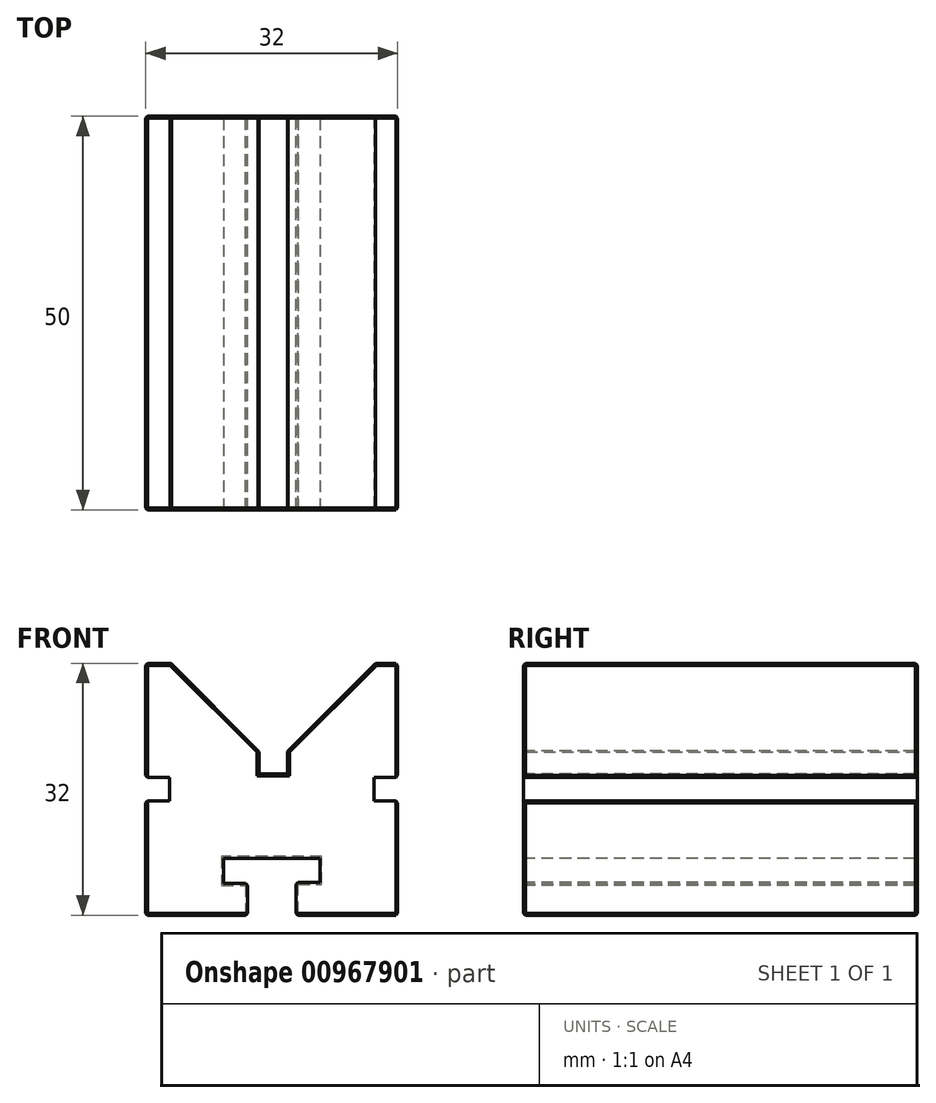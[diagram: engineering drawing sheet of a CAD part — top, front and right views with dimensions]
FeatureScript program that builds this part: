
annotation { "Feature Type Name" : "Feature", "Feature Type Description" : "" }
export const myFeature = defineFeature(function(context is Context, id is Id, definition is map)
    precondition{}
    {
        {
            var Q0;
            Q0=qCreatedBy(makeId("Front.planeOp"),FACE);
            var sketch = newSketch(context, id + "F0", { "sketchPlane" : qUnion([Q0])});
            skLineSegment(sketch, "E0", {"start": v(0, 0) * mm, "end": v(32, 0) * mm});
            skLineSegment(sketch, "E1", {"start": v(32, 0) * mm, "end": v(32, 32) * mm});
            skLineSegment(sketch, "E2", {"start": v(32, 32) * mm, "end": v(29.18, 32) * mm});
            skLineSegment(sketch, "E3", {"start": v(29.18, 32) * mm, "end": v(18, 20.82) * mm});
            skLineSegment(sketch, "E4", {"start": v(18, 20.82) * mm, "end": v(18, 17.96) * mm});
            skLineSegment(sketch, "E5", {"start": v(18, 17.96) * mm, "end": v(14.36, 17.96) * mm});
            skLineSegment(sketch, "E6", {"start": v(14.36, 17.96) * mm, "end": v(14.36, 20.82) * mm});
            skLineSegment(sketch, "E7", {"start": v(14.36, 20.82) * mm, "end": v(3.18, 32) * mm});
            skLineSegment(sketch, "E8", {"start": v(3.18, 32) * mm, "end": v(0, 32) * mm});
            skLineSegment(sketch, "E9", {"start": v(0, 32) * mm, "end": v(0, 0) * mm});
            skLineSegment(sketch, "E10", {"start": v(29.18, 32) * mm, "end": v(16.18, 19) * mm});
            skLineSegment(sketch, "E11", {"start": v(16.18, 19) * mm, "end": v(3.18, 32) * mm});
            skLineSegment(sketch, "E12", {"start": v(3.24, 35.24) * mm, "end": v(0, 32) * mm});
            skSolve(sketch);
        }
        {
            var Q0;
            Q0=makeQuery(id+"F0.imprint","IMPRINT",FACE,{"disambiguationData":[TD([[makeQuery(id+"F0.imprint","IMPRINT",EDGE,{"derivedFrom":sQuery(id+"F0.wireOp",EDGE,"E0")}),1.0]])]});
            extrude(context, id + "F1", {"entities" : qUnion([Q0]), "oppositeDirection" : true, "depth" : 50 * mm, "offsetDistance" : 25 * mm});
        }
        {
            var Q0;
            Q0=qCreatedBy(makeId("Front.planeOp"),FACE);
            var sketch = newSketch(context, id + "F2", { "sketchPlane" : qUnion([Q0])});
            skLineSegment(sketch, "E13", {"start": v(9.9, 7.2) * mm, "end": v(22.1, 7.2) * mm});
            skLineSegment(sketch, "E14", {"start": v(22.1, 7.2) * mm, "end": v(22.1, 4.2) * mm});
            skLineSegment(sketch, "E15", {"start": v(22.1, 4.2) * mm, "end": v(19.1, 4.2) * mm});
            skLineSegment(sketch, "E16", {"start": v(19.1, 4.2) * mm, "end": v(19.1, -5.87) * mm});
            skLineSegment(sketch, "E17", {"start": v(19.1, -5.87) * mm, "end": v(12.9, -5.87) * mm});
            skLineSegment(sketch, "E18", {"start": v(12.9, -5.87) * mm, "end": v(12.9, 4.07) * mm});
            skLineSegment(sketch, "E19", {"start": v(12.9, 4.07) * mm, "end": v(9.9, 4.07) * mm});
            skLineSegment(sketch, "E20", {"start": v(9.9, 4.07) * mm, "end": v(9.9, 7.2) * mm});
            skSolve(sketch);
        }
        {
            var Q0;
            Q0 = qSketchRegion(id + "F2", true);
            extrude(context, id + "F3", {"entities" : qUnion([Q0]), "operationType" : NewBodyOperationType.REMOVE, "oppositeDirection" : true, "depth" : 55 * mm, "offsetDistance" : 25 * mm});
        }
        {
            var Q0;
            Q0=qCreatedBy(makeId("Front.planeOp"),FACE);
            var sketch = newSketch(context, id + "F4", { "sketchPlane" : qUnion([Q0])});
            skLineSegment(sketch, "E21", {"start": v(29, 17.5) * mm, "end": v(29, 14.5) * mm});
            skLineSegment(sketch, "E22", {"start": v(29, 14.5) * mm, "end": v(35.37, 14.5) * mm});
            skLineSegment(sketch, "E23", {"start": v(35.37, 14.5) * mm, "end": v(35.37, 17.5) * mm});
            skLineSegment(sketch, "E24", {"start": v(35.37, 17.5) * mm, "end": v(29, 17.5) * mm});
            skLineSegment(sketch, "E25", {"start": v(-2.73, 17.5) * mm, "end": v(3, 17.5) * mm});
            skLineSegment(sketch, "E26", {"start": v(3, 17.5) * mm, "end": v(3, 14.5) * mm});
            skLineSegment(sketch, "E27", {"start": v(3, 14.5) * mm, "end": v(-2.73, 14.5) * mm});
            skLineSegment(sketch, "E28", {"start": v(-2.73, 14.5) * mm, "end": v(-2.73, 17.5) * mm});
            skSolve(sketch);
        }
        {
            var Q0;
            Q0 = qSketchRegion(id + "F4", true);
            extrude(context, id + "F5", {"entities" : qUnion([Q0]), "operationType" : NewBodyOperationType.REMOVE, "oppositeDirection" : true, "depth" : 50 * mm, "offsetDistance" : 25 * mm});
        }
        {
            var Q0;
            Q0=makeQuery(id+"F1.opExtrude","SWEPT_EDGE",EDGE,{"disambiguationData":[OSD([sQuery(id+"F0.wireOp",EDGE,"E1"),sQuery(id+"F0.wireOp",EDGE,"E2")])]});
            var Q1;
            {var subQ0=sQuery(id+"F0.wireOp",EDGE,"E2");var subQ1=sQuery(id+"F0.wireOp",EDGE,"E1");Q1=makeQuery(id+"F5.boolean.opBoolean","SPLIT",EDGE,{"disambiguationData":[TD([makeQuery(id+"F1.opExtrude","SWEPT_FACE",FACE,{"disambiguationData":[OSD([subQ0])]})])],"derivedFrom":makeQuery(id+"F1.opExtrude","CAP_EDGE",EDGE,{"disambiguationData":[OSD([subQ1])],"isStart":false})});}
            var Q2;
            {var subQ0=sQuery(id+"F0.wireOp",EDGE,"E0");var subQ1=sQuery(id+"F0.wireOp",EDGE,"E1");Q2=makeQuery(id+"F5.boolean.opBoolean","SPLIT",EDGE,{"disambiguationData":[TD([makeQuery(id+"F1.opExtrude","SWEPT_FACE",FACE,{"disambiguationData":[OSD([subQ0])]})])],"derivedFrom":makeQuery(id+"F1.opExtrude","CAP_EDGE",EDGE,{"disambiguationData":[OSD([subQ1])],"isStart":false})});}
            var Q3;
            Q3=makeQuery(id+"F1.opExtrude","SWEPT_EDGE",EDGE,{"disambiguationData":[OSD([sQuery(id+"F0.wireOp",EDGE,"E0"),sQuery(id+"F0.wireOp",EDGE,"E1")])]});
            var Q4;
            {var subQ0=sQuery(id+"F0.wireOp",EDGE,"E0");var subQ1=sQuery(id+"F0.wireOp",EDGE,"E1");Q4=makeQuery(id+"F5.boolean.opBoolean","SPLIT",EDGE,{"disambiguationData":[TD([makeQuery(id+"F1.opExtrude","SWEPT_FACE",FACE,{"disambiguationData":[OSD([subQ0])]})])],"derivedFrom":makeQuery(id+"F1.opExtrude","CAP_EDGE",EDGE,{"disambiguationData":[OSD([subQ1])],"isStart":true})});}
            var Q5;
            {var subQ0=sQuery(id+"F0.wireOp",EDGE,"E2");var subQ1=sQuery(id+"F0.wireOp",EDGE,"E1");Q5=makeQuery(id+"F5.boolean.opBoolean","SPLIT",EDGE,{"disambiguationData":[TD([makeQuery(id+"F1.opExtrude","SWEPT_FACE",FACE,{"disambiguationData":[OSD([subQ0])]})])],"derivedFrom":makeQuery(id+"F1.opExtrude","CAP_EDGE",EDGE,{"disambiguationData":[OSD([subQ1])],"isStart":true})});}
            var Q6;
            Q6=makeQuery(id+"F5.boolean.opBoolean","INTERSECT",EDGE,{"derivedFrom":[makeQuery(id+"F1.opExtrude","SWEPT_FACE",FACE,{"disambiguationData":[OSD([sQuery(id+"F0.wireOp",EDGE,"E1")])]}),makeQuery(id+"F5.opExtrude","SWEPT_FACE",FACE,{"disambiguationData":[OSD([sQuery(id+"F4.wireOp",EDGE,"E24")])]})]});
            var Q7;
            Q7=makeQuery(id+"F5.boolean.opBoolean","INTERSECT",EDGE,{"derivedFrom":[makeQuery(id+"F1.opExtrude","SWEPT_FACE",FACE,{"disambiguationData":[OSD([sQuery(id+"F0.wireOp",EDGE,"E1")])]}),makeQuery(id+"F5.opExtrude","SWEPT_FACE",FACE,{"disambiguationData":[OSD([sQuery(id+"F4.wireOp",EDGE,"E22")])]})]});
            var Q8;
            Q8=makeQuery(id+"F5.boolean.opBoolean","COPY",EDGE,{"derivedFrom":makeQuery(id+"F5.opExtrude","CAP_EDGE",EDGE,{"disambiguationData":[OSD([sQuery(id+"F4.wireOp",EDGE,"E24")])],"isStart":false})});
            var Q9;
            Q9=makeQuery(id+"F5.boolean.opBoolean","COPY",EDGE,{"derivedFrom":makeQuery(id+"F5.opExtrude","CAP_EDGE",EDGE,{"disambiguationData":[OSD([sQuery(id+"F4.wireOp",EDGE,"E22")])],"isStart":false})});
            var Q10;
            Q10=makeQuery(id+"F5.boolean.opBoolean","COPY",EDGE,{"derivedFrom":makeQuery(id+"F5.opExtrude","CAP_EDGE",EDGE,{"disambiguationData":[OSD([sQuery(id+"F4.wireOp",EDGE,"E21")])],"isStart":false})});
            var Q11;
            {var subQ0=sQuery(id+"F0.wireOp",EDGE,"E0");var subQ1=sQuery(id+"F0.wireOp",EDGE,"E1");Q11=makeQuery(id+"F3.boolean.opBoolean","SPLIT",EDGE,{"disambiguationData":[TD([makeQuery(id+"F1.opExtrude","SWEPT_FACE",FACE,{"disambiguationData":[OSD([subQ1])]})])],"derivedFrom":makeQuery(id+"F1.opExtrude","CAP_EDGE",EDGE,{"disambiguationData":[OSD([subQ0])],"isStart":false})});}
            var Q12;
            Q12=makeQuery(id+"F3.boolean.opBoolean","INTERSECT",EDGE,{"derivedFrom":[makeQuery(id+"F1.opExtrude","CAP_FACE",FACE,{"disambiguationData":[OSD([sQuery(id+"F0.wireOp",EDGE,"E0"),sQuery(id+"F0.wireOp",EDGE,"E1"),sQuery(id+"F0.wireOp",EDGE,"E2"),sQuery(id+"F0.wireOp",EDGE,"E3"),sQuery(id+"F0.wireOp",EDGE,"E4"),sQuery(id+"F0.wireOp",EDGE,"E5"),sQuery(id+"F0.wireOp",EDGE,"E6"),sQuery(id+"F0.wireOp",EDGE,"E7"),sQuery(id+"F0.wireOp",EDGE,"E8"),sQuery(id+"F0.wireOp",EDGE,"E9")])],"isStart":false}),makeQuery(id+"F3.opExtrude","SWEPT_FACE",FACE,{"disambiguationData":[OSD([sQuery(id+"F2.wireOp",EDGE,"E14")])]})]});
            var Q13;
            Q13=makeQuery(id+"F3.boolean.opBoolean","INTERSECT",EDGE,{"derivedFrom":[makeQuery(id+"F1.opExtrude","CAP_FACE",FACE,{"disambiguationData":[OSD([sQuery(id+"F0.wireOp",EDGE,"E0"),sQuery(id+"F0.wireOp",EDGE,"E1"),sQuery(id+"F0.wireOp",EDGE,"E2"),sQuery(id+"F0.wireOp",EDGE,"E3"),sQuery(id+"F0.wireOp",EDGE,"E4"),sQuery(id+"F0.wireOp",EDGE,"E5"),sQuery(id+"F0.wireOp",EDGE,"E6"),sQuery(id+"F0.wireOp",EDGE,"E7"),sQuery(id+"F0.wireOp",EDGE,"E8"),sQuery(id+"F0.wireOp",EDGE,"E9")])],"isStart":false}),makeQuery(id+"F3.opExtrude","SWEPT_FACE",FACE,{"disambiguationData":[OSD([sQuery(id+"F2.wireOp",EDGE,"E13")])]})]});
            var Q14;
            Q14=makeQuery(id+"F3.boolean.opBoolean","INTERSECT",EDGE,{"derivedFrom":[makeQuery(id+"F1.opExtrude","CAP_FACE",FACE,{"disambiguationData":[OSD([sQuery(id+"F0.wireOp",EDGE,"E0"),sQuery(id+"F0.wireOp",EDGE,"E1"),sQuery(id+"F0.wireOp",EDGE,"E2"),sQuery(id+"F0.wireOp",EDGE,"E3"),sQuery(id+"F0.wireOp",EDGE,"E4"),sQuery(id+"F0.wireOp",EDGE,"E5"),sQuery(id+"F0.wireOp",EDGE,"E6"),sQuery(id+"F0.wireOp",EDGE,"E7"),sQuery(id+"F0.wireOp",EDGE,"E8"),sQuery(id+"F0.wireOp",EDGE,"E9")])],"isStart":false}),makeQuery(id+"F3.opExtrude","SWEPT_FACE",FACE,{"disambiguationData":[OSD([sQuery(id+"F2.wireOp",EDGE,"E20")])]})]});
            var Q15;
            Q15=makeQuery(id+"F3.boolean.opBoolean","INTERSECT",EDGE,{"derivedFrom":[makeQuery(id+"F1.opExtrude","CAP_FACE",FACE,{"disambiguationData":[OSD([sQuery(id+"F0.wireOp",EDGE,"E0"),sQuery(id+"F0.wireOp",EDGE,"E1"),sQuery(id+"F0.wireOp",EDGE,"E2"),sQuery(id+"F0.wireOp",EDGE,"E3"),sQuery(id+"F0.wireOp",EDGE,"E4"),sQuery(id+"F0.wireOp",EDGE,"E5"),sQuery(id+"F0.wireOp",EDGE,"E6"),sQuery(id+"F0.wireOp",EDGE,"E7"),sQuery(id+"F0.wireOp",EDGE,"E8"),sQuery(id+"F0.wireOp",EDGE,"E9")])],"isStart":false}),makeQuery(id+"F3.opExtrude","SWEPT_FACE",FACE,{"disambiguationData":[OSD([sQuery(id+"F2.wireOp",EDGE,"E19")])]})]});
            var Q16;
            Q16=makeQuery(id+"F3.boolean.opBoolean","INTERSECT",EDGE,{"derivedFrom":[makeQuery(id+"F1.opExtrude","CAP_FACE",FACE,{"disambiguationData":[OSD([sQuery(id+"F0.wireOp",EDGE,"E0"),sQuery(id+"F0.wireOp",EDGE,"E1"),sQuery(id+"F0.wireOp",EDGE,"E2"),sQuery(id+"F0.wireOp",EDGE,"E3"),sQuery(id+"F0.wireOp",EDGE,"E4"),sQuery(id+"F0.wireOp",EDGE,"E5"),sQuery(id+"F0.wireOp",EDGE,"E6"),sQuery(id+"F0.wireOp",EDGE,"E7"),sQuery(id+"F0.wireOp",EDGE,"E8"),sQuery(id+"F0.wireOp",EDGE,"E9")])],"isStart":false}),makeQuery(id+"F3.opExtrude","SWEPT_FACE",FACE,{"disambiguationData":[OSD([sQuery(id+"F2.wireOp",EDGE,"E18")])]})]});
            var Q17;
            Q17=makeQuery(id+"F3.boolean.opBoolean","INTERSECT",EDGE,{"derivedFrom":[makeQuery(id+"F1.opExtrude","CAP_FACE",FACE,{"disambiguationData":[OSD([sQuery(id+"F0.wireOp",EDGE,"E0"),sQuery(id+"F0.wireOp",EDGE,"E1"),sQuery(id+"F0.wireOp",EDGE,"E2"),sQuery(id+"F0.wireOp",EDGE,"E3"),sQuery(id+"F0.wireOp",EDGE,"E4"),sQuery(id+"F0.wireOp",EDGE,"E5"),sQuery(id+"F0.wireOp",EDGE,"E6"),sQuery(id+"F0.wireOp",EDGE,"E7"),sQuery(id+"F0.wireOp",EDGE,"E8"),sQuery(id+"F0.wireOp",EDGE,"E9")])],"isStart":false}),makeQuery(id+"F3.opExtrude","SWEPT_FACE",FACE,{"disambiguationData":[OSD([sQuery(id+"F2.wireOp",EDGE,"E16")])]})]});
            var Q18;
            Q18=makeQuery(id+"F3.boolean.opBoolean","INTERSECT",EDGE,{"derivedFrom":[makeQuery(id+"F1.opExtrude","CAP_FACE",FACE,{"disambiguationData":[OSD([sQuery(id+"F0.wireOp",EDGE,"E0"),sQuery(id+"F0.wireOp",EDGE,"E1"),sQuery(id+"F0.wireOp",EDGE,"E2"),sQuery(id+"F0.wireOp",EDGE,"E3"),sQuery(id+"F0.wireOp",EDGE,"E4"),sQuery(id+"F0.wireOp",EDGE,"E5"),sQuery(id+"F0.wireOp",EDGE,"E6"),sQuery(id+"F0.wireOp",EDGE,"E7"),sQuery(id+"F0.wireOp",EDGE,"E8"),sQuery(id+"F0.wireOp",EDGE,"E9")])],"isStart":false}),makeQuery(id+"F3.opExtrude","SWEPT_FACE",FACE,{"disambiguationData":[OSD([sQuery(id+"F2.wireOp",EDGE,"E15")])]})]});
            var Q19;
            {var subQ0=sQuery(id+"F0.wireOp",EDGE,"E0");var subQ1=sQuery(id+"F0.wireOp",EDGE,"E9");Q19=makeQuery(id+"F3.boolean.opBoolean","SPLIT",EDGE,{"disambiguationData":[TD([makeQuery(id+"F1.opExtrude","SWEPT_FACE",FACE,{"disambiguationData":[OSD([subQ1])]})])],"derivedFrom":makeQuery(id+"F1.opExtrude","CAP_EDGE",EDGE,{"disambiguationData":[OSD([subQ0])],"isStart":false})});}
            var Q20;
            {var subQ0=sQuery(id+"F0.wireOp",EDGE,"E0");var subQ1=sQuery(id+"F0.wireOp",EDGE,"E9");Q20=makeQuery(id+"F5.boolean.opBoolean","SPLIT",EDGE,{"disambiguationData":[TD([makeQuery(id+"F1.opExtrude","SWEPT_FACE",FACE,{"disambiguationData":[OSD([subQ0])]})])],"derivedFrom":makeQuery(id+"F1.opExtrude","CAP_EDGE",EDGE,{"disambiguationData":[OSD([subQ1])],"isStart":false})});}
            var Q21;
            Q21=makeQuery(id+"F1.opExtrude","SWEPT_EDGE",EDGE,{"disambiguationData":[OSD([sQuery(id+"F0.wireOp",EDGE,"E0"),sQuery(id+"F0.wireOp",EDGE,"E9")])]});
            var Q22;
            {var subQ0=sQuery(id+"F0.wireOp",EDGE,"E0");var subQ1=sQuery(id+"F0.wireOp",EDGE,"E9");Q22=makeQuery(id+"F5.boolean.opBoolean","SPLIT",EDGE,{"disambiguationData":[TD([makeQuery(id+"F1.opExtrude","SWEPT_FACE",FACE,{"disambiguationData":[OSD([subQ0])]})])],"derivedFrom":makeQuery(id+"F1.opExtrude","CAP_EDGE",EDGE,{"disambiguationData":[OSD([subQ1])],"isStart":true})});}
            var Q23;
            Q23=makeQuery(id+"F5.boolean.opBoolean","INTERSECT",EDGE,{"derivedFrom":[makeQuery(id+"F1.opExtrude","SWEPT_FACE",FACE,{"disambiguationData":[OSD([sQuery(id+"F0.wireOp",EDGE,"E9")])]}),makeQuery(id+"F5.opExtrude","SWEPT_FACE",FACE,{"disambiguationData":[OSD([sQuery(id+"F4.wireOp",EDGE,"E27")])]})]});
            var Q24;
            Q24=makeQuery(id+"F5.boolean.opBoolean","COPY",EDGE,{"derivedFrom":makeQuery(id+"F5.opExtrude","CAP_EDGE",EDGE,{"disambiguationData":[OSD([sQuery(id+"F4.wireOp",EDGE,"E25")])],"isStart":false})});
            var Q25;
            Q25=makeQuery(id+"F5.boolean.opBoolean","COPY",EDGE,{"derivedFrom":makeQuery(id+"F5.opExtrude","CAP_EDGE",EDGE,{"disambiguationData":[OSD([sQuery(id+"F4.wireOp",EDGE,"E26")])],"isStart":false})});
            var Q26;
            Q26=makeQuery(id+"F5.boolean.opBoolean","COPY",EDGE,{"derivedFrom":makeQuery(id+"F5.opExtrude","CAP_EDGE",EDGE,{"disambiguationData":[OSD([sQuery(id+"F4.wireOp",EDGE,"E27")])],"isStart":false})});
            var Q27;
            {var subQ0=sQuery(id+"F0.wireOp",EDGE,"E9");var subQ1=sQuery(id+"F0.wireOp",EDGE,"E8");Q27=makeQuery(id+"F5.boolean.opBoolean","SPLIT",EDGE,{"disambiguationData":[TD([makeQuery(id+"F1.opExtrude","SWEPT_FACE",FACE,{"disambiguationData":[OSD([subQ1])]})])],"derivedFrom":makeQuery(id+"F1.opExtrude","CAP_EDGE",EDGE,{"disambiguationData":[OSD([subQ0])],"isStart":false})});}
            var Q28;
            Q28=makeQuery(id+"F1.opExtrude","CAP_EDGE",EDGE,{"disambiguationData":[OSD([sQuery(id+"F0.wireOp",EDGE,"E8")])],"isStart":false});
            var Q29;
            Q29=makeQuery(id+"F1.opExtrude","CAP_EDGE",EDGE,{"disambiguationData":[OSD([sQuery(id+"F0.wireOp",EDGE,"E7")])],"isStart":false});
            var Q30;
            Q30=makeQuery(id+"F1.opExtrude","CAP_EDGE",EDGE,{"disambiguationData":[OSD([sQuery(id+"F0.wireOp",EDGE,"E6")])],"isStart":false});
            var Q31;
            Q31=makeQuery(id+"F1.opExtrude","CAP_EDGE",EDGE,{"disambiguationData":[OSD([sQuery(id+"F0.wireOp",EDGE,"E5")])],"isStart":false});
            var Q32;
            Q32=makeQuery(id+"F1.opExtrude","CAP_EDGE",EDGE,{"disambiguationData":[OSD([sQuery(id+"F0.wireOp",EDGE,"E4")])],"isStart":false});
            var Q33;
            Q33=makeQuery(id+"F1.opExtrude","SWEPT_EDGE",EDGE,{"disambiguationData":[OSD([sQuery(id+"F0.wireOp",EDGE,"E3"),sQuery(id+"F0.wireOp",EDGE,"E4")])]});
            var Q34;
            Q34=makeQuery(id+"F1.opExtrude","CAP_EDGE",EDGE,{"disambiguationData":[OSD([sQuery(id+"F0.wireOp",EDGE,"E3")])],"isStart":false});
            var Q35;
            Q35=makeQuery(id+"F1.opExtrude","SWEPT_EDGE",EDGE,{"disambiguationData":[OSD([sQuery(id+"F0.wireOp",EDGE,"E8"),sQuery(id+"F0.wireOp",EDGE,"E9")])]});
            var Q36;
            Q36=makeQuery(id+"F1.opExtrude","SWEPT_EDGE",EDGE,{"disambiguationData":[OSD([sQuery(id+"F0.wireOp",EDGE,"E7"),sQuery(id+"F0.wireOp",EDGE,"E8")])]});
            var Q37;
            Q37=makeQuery(id+"F1.opExtrude","SWEPT_EDGE",EDGE,{"disambiguationData":[OSD([sQuery(id+"F0.wireOp",EDGE,"E6"),sQuery(id+"F0.wireOp",EDGE,"E7")])]});
            var Q38;
            Q38=makeQuery(id+"F1.opExtrude","CAP_EDGE",EDGE,{"disambiguationData":[OSD([sQuery(id+"F0.wireOp",EDGE,"E2")])],"isStart":false});
            chamfer(context, id + "F6", {"entities" : qUnion([Q0, Q1, Q2, Q3, Q4, Q5, Q6, Q7, Q8, Q9, Q10, Q11, Q12, Q13, Q14, Q15, Q16, Q17, Q18, Q19, Q20, Q21, Q22, Q23, Q24, Q25, Q26, Q27, Q28, Q29, Q30, Q31, Q32, Q33, Q34, Q35, Q36, Q37, Q38]), "width" : .25 * mm, "tangentPropagation" : true});
        }
        {
            var Q0;
            Q0=makeQuery(id+"F3.boolean.opBoolean","COPY",EDGE,{"derivedFrom":makeQuery(id+"F3.opExtrude","SWEPT_EDGE",EDGE,{"disambiguationData":[OSD([sQuery(id+"F2.wireOp",EDGE,"E15"),sQuery(id+"F2.wireOp",EDGE,"E16")])]})});
            var Q1;
            Q1=makeQuery(id+"F3.boolean.opBoolean","INTERSECT",EDGE,{"derivedFrom":[makeQuery(id+"F1.opExtrude","SWEPT_FACE",FACE,{"disambiguationData":[OSD([sQuery(id+"F0.wireOp",EDGE,"E0")])]}),makeQuery(id+"F3.opExtrude","SWEPT_FACE",FACE,{"disambiguationData":[OSD([sQuery(id+"F2.wireOp",EDGE,"E16")])]})]});
            var Q2;
            Q2=makeQuery(id+"F3.boolean.opBoolean","COPY",EDGE,{"derivedFrom":makeQuery(id+"F3.opExtrude","CAP_EDGE",EDGE,{"disambiguationData":[OSD([sQuery(id+"F2.wireOp",EDGE,"E16")])],"isStart":true})});
            var Q3;
            Q3=makeQuery(id+"F3.boolean.opBoolean","INTERSECT",EDGE,{"derivedFrom":[makeQuery(id+"F1.opExtrude","SWEPT_FACE",FACE,{"disambiguationData":[OSD([sQuery(id+"F0.wireOp",EDGE,"E0")])]}),makeQuery(id+"F3.opExtrude","SWEPT_FACE",FACE,{"disambiguationData":[OSD([sQuery(id+"F2.wireOp",EDGE,"E18")])]})]});
            var Q4;
            Q4=makeQuery(id+"F3.boolean.opBoolean","COPY",EDGE,{"derivedFrom":makeQuery(id+"F3.opExtrude","SWEPT_EDGE",EDGE,{"disambiguationData":[OSD([sQuery(id+"F2.wireOp",EDGE,"E18"),sQuery(id+"F2.wireOp",EDGE,"E19")])]})});
            var Q5;
            Q5=makeQuery(id+"F3.boolean.opBoolean","COPY",EDGE,{"derivedFrom":makeQuery(id+"F3.opExtrude","CAP_EDGE",EDGE,{"disambiguationData":[OSD([sQuery(id+"F2.wireOp",EDGE,"E18")])],"isStart":true})});
            var Q6;
            Q6=makeQuery(id+"F3.boolean.opBoolean","COPY",EDGE,{"derivedFrom":makeQuery(id+"F3.opExtrude","CAP_EDGE",EDGE,{"disambiguationData":[OSD([sQuery(id+"F2.wireOp",EDGE,"E13")])],"isStart":true})});
            var Q7;
            Q7=makeQuery(id+"F3.boolean.opBoolean","COPY",EDGE,{"derivedFrom":makeQuery(id+"F3.opExtrude","CAP_EDGE",EDGE,{"disambiguationData":[OSD([sQuery(id+"F2.wireOp",EDGE,"E20")])],"isStart":true})});
            var Q8;
            Q8=makeQuery(id+"F3.boolean.opBoolean","COPY",EDGE,{"derivedFrom":makeQuery(id+"F3.opExtrude","CAP_EDGE",EDGE,{"disambiguationData":[OSD([sQuery(id+"F2.wireOp",EDGE,"E19")])],"isStart":true})});
            var Q9;
            Q9=makeQuery(id+"F3.boolean.opBoolean","COPY",EDGE,{"derivedFrom":makeQuery(id+"F3.opExtrude","CAP_EDGE",EDGE,{"disambiguationData":[OSD([sQuery(id+"F2.wireOp",EDGE,"E15")])],"isStart":true})});
            var Q10;
            Q10=makeQuery(id+"F3.boolean.opBoolean","COPY",EDGE,{"derivedFrom":makeQuery(id+"F3.opExtrude","CAP_EDGE",EDGE,{"disambiguationData":[OSD([sQuery(id+"F2.wireOp",EDGE,"E14")])],"isStart":true})});
            var Q11;
            {var subQ0=sQuery(id+"F0.wireOp",EDGE,"E0");var subQ1=sQuery(id+"F0.wireOp",EDGE,"E1");Q11=makeQuery(id+"F3.boolean.opBoolean","SPLIT",EDGE,{"disambiguationData":[TD([makeQuery(id+"F1.opExtrude","SWEPT_FACE",FACE,{"disambiguationData":[OSD([subQ1])]})])],"derivedFrom":makeQuery(id+"F1.opExtrude","CAP_EDGE",EDGE,{"disambiguationData":[OSD([subQ0])],"isStart":true})});}
            var Q12;
            {var subQ0=sQuery(id+"F0.wireOp",EDGE,"E0");var subQ1=sQuery(id+"F0.wireOp",EDGE,"E9");Q12=makeQuery(id+"F3.boolean.opBoolean","SPLIT",EDGE,{"disambiguationData":[TD([makeQuery(id+"F1.opExtrude","SWEPT_FACE",FACE,{"disambiguationData":[OSD([subQ1])]})])],"derivedFrom":makeQuery(id+"F1.opExtrude","CAP_EDGE",EDGE,{"disambiguationData":[OSD([subQ0])],"isStart":true})});}
            var Q13;
            Q13=makeQuery(id+"F5.boolean.opBoolean","COPY",EDGE,{"derivedFrom":makeQuery(id+"F5.opExtrude","CAP_EDGE",EDGE,{"disambiguationData":[OSD([sQuery(id+"F4.wireOp",EDGE,"E27")])],"isStart":true})});
            var Q14;
            Q14=makeQuery(id+"F5.boolean.opBoolean","COPY",EDGE,{"derivedFrom":makeQuery(id+"F5.opExtrude","CAP_EDGE",EDGE,{"disambiguationData":[OSD([sQuery(id+"F4.wireOp",EDGE,"E26")])],"isStart":true})});
            var Q15;
            Q15=makeQuery(id+"F5.boolean.opBoolean","COPY",EDGE,{"derivedFrom":makeQuery(id+"F5.opExtrude","CAP_EDGE",EDGE,{"disambiguationData":[OSD([sQuery(id+"F4.wireOp",EDGE,"E25")])],"isStart":true})});
            var Q16;
            {var subQ0=sQuery(id+"F0.wireOp",EDGE,"E9");var subQ1=sQuery(id+"F0.wireOp",EDGE,"E8");Q16=makeQuery(id+"F5.boolean.opBoolean","SPLIT",EDGE,{"disambiguationData":[TD([makeQuery(id+"F1.opExtrude","SWEPT_FACE",FACE,{"disambiguationData":[OSD([subQ1])]})])],"derivedFrom":makeQuery(id+"F1.opExtrude","CAP_EDGE",EDGE,{"disambiguationData":[OSD([subQ0])],"isStart":true})});}
            var Q17;
            Q17=makeQuery(id+"F5.boolean.opBoolean","INTERSECT",EDGE,{"derivedFrom":[makeQuery(id+"F1.opExtrude","SWEPT_FACE",FACE,{"disambiguationData":[OSD([sQuery(id+"F0.wireOp",EDGE,"E9")])]}),makeQuery(id+"F5.opExtrude","SWEPT_FACE",FACE,{"disambiguationData":[OSD([sQuery(id+"F4.wireOp",EDGE,"E25")])]})]});
            var Q18;
            Q18=makeQuery(id+"F1.opExtrude","CAP_EDGE",EDGE,{"disambiguationData":[OSD([sQuery(id+"F0.wireOp",EDGE,"E5")])],"isStart":true});
            var Q19;
            Q19=makeQuery(id+"F1.opExtrude","CAP_EDGE",EDGE,{"disambiguationData":[OSD([sQuery(id+"F0.wireOp",EDGE,"E6")])],"isStart":true});
            var Q20;
            Q20=makeQuery(id+"F1.opExtrude","CAP_EDGE",EDGE,{"disambiguationData":[OSD([sQuery(id+"F0.wireOp",EDGE,"E4")])],"isStart":true});
            var Q21;
            Q21=makeQuery(id+"F1.opExtrude","CAP_EDGE",EDGE,{"disambiguationData":[OSD([sQuery(id+"F0.wireOp",EDGE,"E7")])],"isStart":true});
            var Q22;
            Q22=makeQuery(id+"F1.opExtrude","CAP_EDGE",EDGE,{"disambiguationData":[OSD([sQuery(id+"F0.wireOp",EDGE,"E3")])],"isStart":true});
            var Q23;
            Q23=makeQuery(id+"F1.opExtrude","CAP_EDGE",EDGE,{"disambiguationData":[OSD([sQuery(id+"F0.wireOp",EDGE,"E8")])],"isStart":true});
            var Q24;
            Q24=makeQuery(id+"F1.opExtrude","CAP_EDGE",EDGE,{"disambiguationData":[OSD([sQuery(id+"F0.wireOp",EDGE,"E2")])],"isStart":true});
            var Q25;
            Q25=makeQuery(id+"F5.boolean.opBoolean","COPY",EDGE,{"derivedFrom":makeQuery(id+"F5.opExtrude","CAP_EDGE",EDGE,{"disambiguationData":[OSD([sQuery(id+"F4.wireOp",EDGE,"E24")])],"isStart":true})});
            var Q26;
            Q26=makeQuery(id+"F5.boolean.opBoolean","COPY",EDGE,{"derivedFrom":makeQuery(id+"F5.opExtrude","CAP_EDGE",EDGE,{"disambiguationData":[OSD([sQuery(id+"F4.wireOp",EDGE,"E21")])],"isStart":true})});
            var Q27;
            Q27=makeQuery(id+"F5.boolean.opBoolean","COPY",EDGE,{"derivedFrom":makeQuery(id+"F5.opExtrude","CAP_EDGE",EDGE,{"disambiguationData":[OSD([sQuery(id+"F4.wireOp",EDGE,"E22")])],"isStart":true})});
            chamfer(context, id + "F7", {"entities" : qUnion([Q0, Q1, Q2, Q3, Q4, Q5, Q6, Q7, Q8, Q9, Q10, Q11, Q12, Q13, Q14, Q15, Q16, Q17, Q18, Q19, Q20, Q21, Q22, Q23, Q24, Q25, Q26, Q27]), "width" : .25 * mm, "tangentPropagation" : true});
        }
    });
